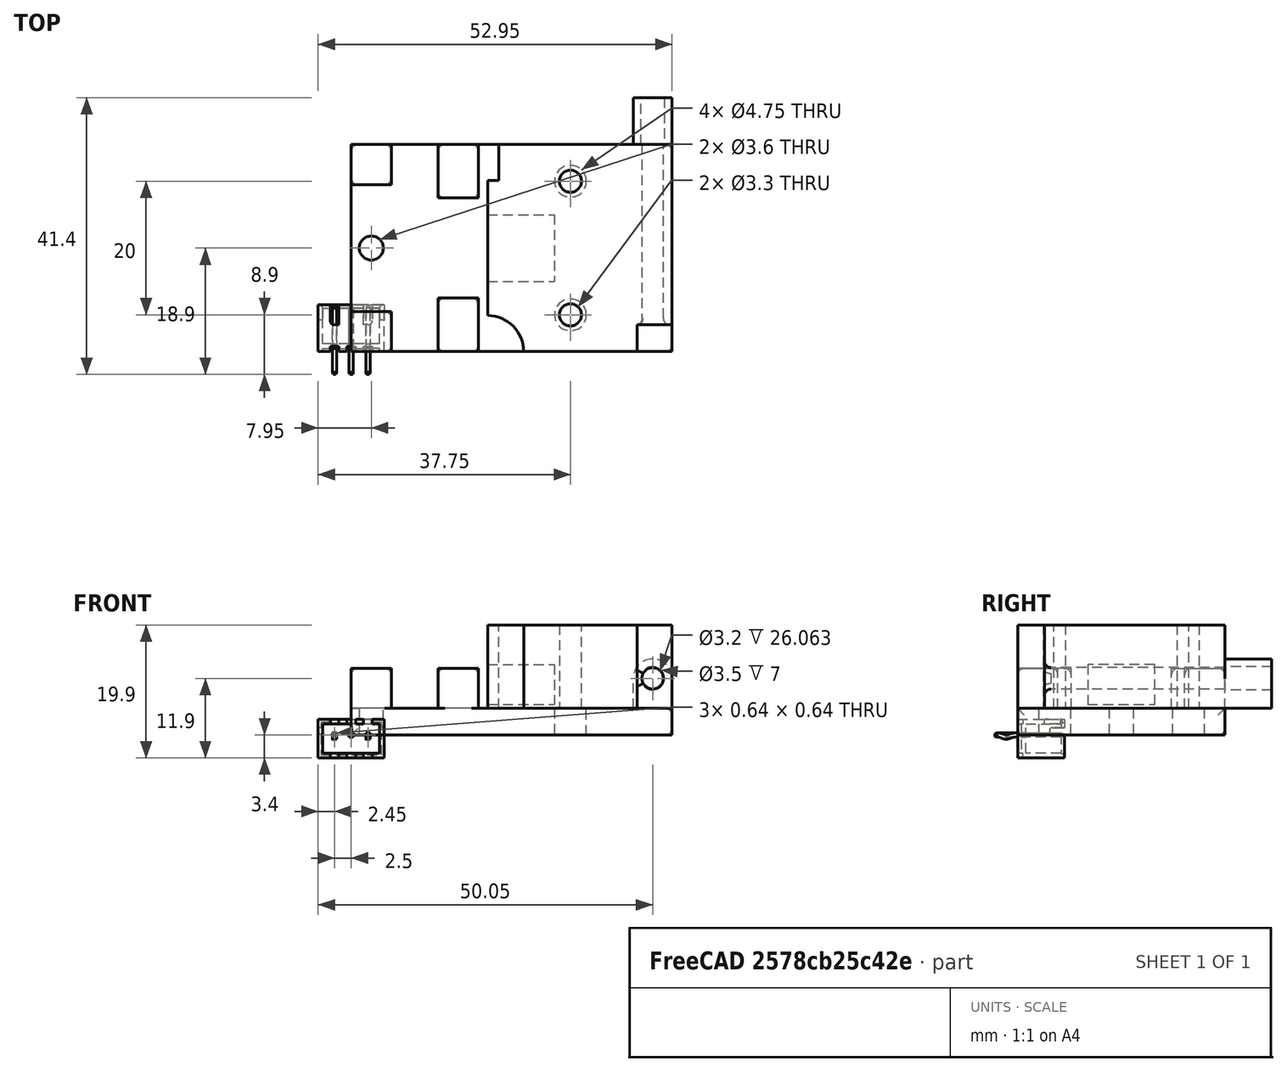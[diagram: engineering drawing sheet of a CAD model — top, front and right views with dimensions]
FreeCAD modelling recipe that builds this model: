
FCSTD DOCUMENT  (FreeCAD 0.19R24291 (Git))
Label: Filament Sensor Mount
License: All rights reserved
LicenseURL: http://en.wikipedia.org/wiki/All_rights_reserved
objects: Sketcher::SketchObject×6, PartDesign::Pad×4, Part::Feature×4, PartDesign::Body×2, PartDesign::Pocket×2, Mesh::Feature×1, Part::Fillet×1, App::Part×1, PartDesign::Fillet×1
note: 27 computed .brp shape members not serialized (recipe doc carries the construction recipe); baked Part::Feature solids carry a one-line shape summary decoded from their .brp

FEATURE [Mesh::Feature] bowen_retainer
  Placement = pos=(-107.25,-102,0) rot=(0,0,1;0rad)
FEATURE [Sketcher::SketchObject] Sketch
  FullyConstrained = true
  MapMode = 5
  Support = -> [XY_Plane]
  sketch-geometry (9):
    g0: LineSegment StartX=0 StartY=0 StartZ=0 EndX=48 EndY=0 EndZ=0
    g1: LineSegment StartX=48 StartY=0 StartZ=0 EndX=48 EndY=31 EndZ=0
    g2: LineSegment StartX=48 StartY=31 StartZ=0 EndX=0 EndY=31 EndZ=0
    g3: LineSegment StartX=0 StartY=31 StartZ=0 EndX=0 EndY=0 EndZ=0
    g4: Circle CenterX=3 CenterY=15.5 CenterZ=0 NormalX=0 NormalY=0 NormalZ=1 AngleXU=0 Radius=1.8
    g5: Circle CenterX=32.8 CenterY=25.5 CenterZ=0 NormalX=0 NormalY=0 NormalZ=1 AngleXU=0 Radius=2.375
    g6: Circle CenterX=32.8 CenterY=5.5 CenterZ=0 NormalX=0 NormalY=0 NormalZ=1 AngleXU=0 Radius=2.375
    g7: LineSegment StartX=19.5 StartY=31 StartZ=0 EndX=19.5 EndY=0 EndZ=0
    g8: LineSegment StartX=13 StartY=31 StartZ=0 EndX=13 EndY=0 EndZ=0
  constraints (28):
    c: Coincident(g0,g1)
    c: Coincident(g1,g2)
    c: Coincident(g2,g3)
    c: Coincident(g3,g0)
    c: Horizontal(g0)
    c: Horizontal(g2)
    c: Vertical(g1)
    c: Vertical(g3)
    c: Coincident(g0,g-1)
    c: DistanceX(g0,g0) = 48
    c: DistanceY(g1,g1) = 31
    c: Radius(g4) = 1.8
    c: DistanceX(g0,g4) = 3
    c: DistanceY(g0,g4) = 15.5
    c: Radius(g5) = 2.375
    c: Equal(g5,g6)
    c: DistanceX(g6,g0) = 15.2
    c: Vertical(g6,g5)
    c: DistanceY(g6,g5) = 20
    c: DistanceY(g5,g1) = 5.5
    c: PointOnObject(g7,g2)
    c: PointOnObject(g7,g0)
    c: Vertical(g7)
    c: DistanceX(g7,g1) = 28.5
    c: PointOnObject(g8,g2)
    c: PointOnObject(g8,g0)
    c: Vertical(g8)
    c: DistanceX(g2,g8) = 13
FEATURE [PartDesign::Pad] Pad
  Direction = (1,1,1)
  Length = 4
  Length2 = 100
  Profile = -> Sketch
  Type = 0
FEATURE [Sketcher::SketchObject] Sketch001
  ExternalGeometry = -> [Pad]
  FullyConstrained = true
  MapMode = 5
  Placement = pos=(0,0,4) rot=(0,0,1;0rad)
  Support = -> [Pad]
  sketch-geometry (16):
    g0: LineSegment StartX=0 StartY=0 StartZ=0 EndX=6 EndY=0 EndZ=0
    g1: LineSegment StartX=6 StartY=0 StartZ=0 EndX=6 EndY=6 EndZ=0
    g2: LineSegment StartX=6 StartY=6 StartZ=0 EndX=0 EndY=6 EndZ=0
    g3: LineSegment StartX=0 StartY=6 StartZ=0 EndX=0 EndY=0 EndZ=0
    g4: LineSegment StartX=0 StartY=31 StartZ=0 EndX=6 EndY=31 EndZ=0
    g5: LineSegment StartX=6 StartY=31 StartZ=0 EndX=6 EndY=25 EndZ=0
    g6: LineSegment StartX=6 StartY=25 StartZ=0 EndX=0 EndY=25 EndZ=0
    g7: LineSegment StartX=0 StartY=25 StartZ=0 EndX=0 EndY=31 EndZ=0
    g8: LineSegment StartX=13 StartY=31 StartZ=0 EndX=19 EndY=31 EndZ=0
    g9: LineSegment StartX=19 StartY=31 StartZ=0 EndX=19 EndY=23 EndZ=0
    g10: LineSegment StartX=19 StartY=23 StartZ=0 EndX=13 EndY=23 EndZ=0
    g11: LineSegment StartX=13 StartY=23 StartZ=0 EndX=13 EndY=31 EndZ=0
    g12: LineSegment StartX=13 StartY=0 StartZ=0 EndX=19 EndY=0 EndZ=0
    g13: LineSegment StartX=19 StartY=0 StartZ=0 EndX=19 EndY=8 EndZ=0
    g14: LineSegment StartX=19 StartY=8 StartZ=0 EndX=13 EndY=8 EndZ=0
    g15: LineSegment StartX=13 StartY=8 StartZ=0 EndX=13 EndY=0 EndZ=0
  constraints (47):
    c: Coincident(g0,g1)
    c: Coincident(g1,g2)
    c: Coincident(g2,g3)
    c: Coincident(g3,g0)
    c: Horizontal(g0)
    c: Horizontal(g2)
    c: Vertical(g1)
    c: Vertical(g3)
    c: Coincident(g0,g-1)
    c: Coincident(g4,g5)
    c: Coincident(g5,g6)
    c: Coincident(g6,g7)
    c: Coincident(g7,g4)
    c: Horizontal(g4)
    c: Horizontal(g6)
    c: Vertical(g5)
    c: Vertical(g7)
    c: Coincident(g4,g-3)
    c: DistanceX(g0,g0) = 6
    c: Equal(g0,g3)
    c: Equal(g3,g7)
    c: Equal(g7,g4)
    c: Coincident(g8,g9)
    c: Coincident(g9,g10)
    c: Coincident(g10,g11)
    c: Coincident(g11,g8)
    c: Horizontal(g8)
    c: Horizontal(g10)
    c: Vertical(g9)
    c: Vertical(g11)
    c: PointOnObject(g8,g-3)
    c: Coincident(g12,g13)
    c: Coincident(g13,g14)
    c: Coincident(g14,g15)
    c: Coincident(g15,g12)
    c: Horizontal(g12)
    c: Horizontal(g14)
    c: Vertical(g13)
    c: Vertical(g15)
    c: PointOnObject(g12,g-1)
    c: DistanceY(g15,g15) = 8
    c: Equal(g0,g12)
    c: Equal(g12,g8)
    c: Equal(g15,g11)
    c: DistanceX(g4,g8) = 13
    c: Vertical(g10,g14)
    c: DistanceX(g9,g-3) = 29
FEATURE [PartDesign::Pad] Pad001
  BaseFeature = -> Pad
  Direction = (1,1,1)
  Length = 6
  Length2 = 100
  Profile = -> Sketch001
  Type = 0
FEATURE [PartDesign::Body] Body  label="Filament Sensor Mount"
  Group = -> [Sketch,Pad,Sketch001,Pad001]
  Origin = -> Origin
  Tip = -> Pad001
FEATURE [Part::Fillet] Fillet
  Base = -> Pad001
  Edges = 38 edges r=1: [Edge2,Edge3,Edge13,Edge14,Edge15,Edge16,Edge20,Edge21,Edge22,Edge38,Edge39,Edge40,Edge43,Edge44,Edge45,Edge46,Edge47,Edge51,Edge52,Edge53,Edge54,Edge55,Edge56,Edge57,Edge58,Edge59,Edge60,Edge61,Edge62,Edge63,Edge64,Edge65,Edge66,Edge67,Edge68,Edge69,Edge70,Edge71]
FEATURE [Sketcher::SketchObject] Sketch002
  FullyConstrained = true
  MapMode = 5
  Support = -> [XY_Plane001]
  sketch-geometry (11):
    g0: LineSegment StartX=5.4 StartY=2e-16 StartZ=0 EndX=22.4 EndY=2e-16 EndZ=0
    g1: LineSegment StartX=27.6 StartY=4 StartZ=0 EndX=27.6 EndY=31 EndZ=0
    g2: LineSegment StartX=27.6 StartY=31 StartZ=0 EndX=1.7 EndY=31 EndZ=0
    g3: LineSegment StartX=-3.3e-15 StartY=25.6 StartZ=0 EndX=-3.3e-15 EndY=5.4 EndZ=0
    g4: Circle CenterX=12.4 CenterY=25.5 CenterZ=0 NormalX=0 NormalY=0 NormalZ=1 AngleXU=0 Radius=1.65
    g5: Circle CenterX=12.4 CenterY=5.5 CenterZ=0 NormalX=0 NormalY=0 NormalZ=1 AngleXU=0 Radius=1.65
    g6: LineSegment StartX=22.4 StartY=2e-16 StartZ=0 EndX=22.4 EndY=4 EndZ=0
    g7: LineSegment StartX=22.4 StartY=4 StartZ=0 EndX=27.6 EndY=4 EndZ=0
    g8: LineSegment StartX=-3.3e-15 StartY=25.6 StartZ=0 EndX=1.7 EndY=25.6 EndZ=0
    g9: LineSegment StartX=1.7 StartY=25.6 StartZ=0 EndX=1.7 EndY=31 EndZ=0
    g10: ArcOfCircle CenterX=0 CenterY=0 CenterZ=0 NormalX=0 NormalY=0 NormalZ=1 AngleXU=0 Radius=5.4 StartAngle=0 EndAngle=1.5708
  constraints (33):
    c: Coincident(g1,g2)
    c: Horizontal(g0)
    c: Horizontal(g2)
    c: Vertical(g1)
    c: Vertical(g3)
    c: Radius(g4) = 1.65
    c: Equal(g4,g5)
    c: Vertical(g4,g5)
    c: DistanceY(g5,g4) = 20
    c: Vertical(g6)
    c: Coincident(g7,g6)
    c: Horizontal(g7)
    c: Distance(g6) = 4
    c: Coincident(g0,g6)
    c: Coincident(g1,g7)
    c: DistanceX(g7,g7) = 5.2
    c: DistanceY(g-1,g5) = 5.5
    c: DistanceX(g5,g1) = 15.2
    c: Horizontal(g8)
    c: Coincident(g8,g9)
    c: Vertical(g9)
    c: DistanceY(g9,g9) = 5.4
    c: DistanceX(g8,g8) = 1.7
    c: Coincident(g3,g8)
    c: Coincident(g2,g9)
    c: DistanceY(g-1,g2) = 31
    c: DistanceX(g3,g1) = 27.6
    c: DistanceX(g-1,g10) = 5.4
    c: Coincident(g10,g-1)
    c: Coincident(g3,g10)
    c: Coincident(g0,g10)
    c: DistanceX(g0,g0) = 17
    c: PointOnObject(g0,g-1)
FEATURE [PartDesign::Pad] Pad002
  Direction = (1,1,1)
  Length = 12.5
  Length2 = 100
  Profile = -> Sketch002
  Type = 0
FEATURE [Sketcher::SketchObject] Sketch003
  ExternalGeometry = -> [Pad002]
  FullyConstrained = true
  MapMode = 5
  Placement = pos=(0,31,0) rot=(0,0.707107,0.707107;3.14159rad)
  Support = -> [Pad002]
  sketch-geometry (5):
    g0: LineSegment StartX=-27.6 StartY=0 StartZ=0 EndX=-21.8 EndY=0 EndZ=0
    g1: LineSegment StartX=-21.8 StartY=0 StartZ=0 EndX=-21.8 EndY=4.5 EndZ=0
    g2: LineSegment StartX=-27.6 StartY=4.5 StartZ=0 EndX=-27.6 EndY=0 EndZ=0
    g3: ArcOfCircle CenterX=-24.7 CenterY=4.5 CenterZ=0 NormalX=0 NormalY=0 NormalZ=1 AngleXU=0 Radius=2.9 StartAngle=7.1e-15 EndAngle=3.14159
    g4: Circle CenterX=-24.7 CenterY=4.5 CenterZ=0 NormalX=0 NormalY=0 NormalZ=1 AngleXU=0 Radius=1.75
  constraints (14):
    c: Coincident(g0,g1)
    c: Coincident(g2,g0)
    c: Horizontal(g0)
    c: Vertical(g1)
    c: Vertical(g2)
    c: Coincident(g0,g-3)
    c: DistanceX(g0,g0) = 5.8
    c: Coincident(g3,g1)
    c: Angle(g3) = 3.14159
    c: DistanceY(g2,g2) = 4.5
    c: Coincident(g4,g3)
    c: Radius(g4) = 1.75
    c: Coincident(g3,g2)
    c: Horizontal(g1,g2)
FEATURE [PartDesign::Pad] Pad003
  BaseFeature = -> Pad002
  Direction = (1,1,1)
  Length = 7
  Length2 = 100
  Profile = -> Sketch003
  Type = 0
FEATURE [Part::Feature] Part__Feature  label="B3B-XH-A (LF)(SN)"
  shape: bbox 0.64 x 10.2 x 0.96 mm, 28 faces (baked)
FEATURE [Part::Feature] Part__Feature001  label="B3B-XH-A (LF)(SN)001"
  shape: bbox 9.9 x 7 x 5.75 mm, 95 faces (baked)
FEATURE [Part::Feature] Part__Feature002  label="B3B-XH-A (LF)(SN)002"
  shape: bbox 0.64 x 10.2 x 0.96 mm, 26 faces (baked)
FEATURE [Part::Feature] Part__Feature003  label="B3B-XH-A (LF)(SN)003"
  shape: bbox 0.64 x 10.2 x 0.64 mm, 14 faces (baked)
FEATURE [App::Part] B3B_XH_A__LF__SN_  label="B3B-XH-A (LF)(SN)004"
  Group = -> [Part__Feature,Part__Feature001,Part__Feature002,Part__Feature003]
  Origin = -> Origin002
  Placement = pos=(27,15.5,7) rot=(-0.707107,0.707107,0;3.14159rad)
FEATURE [Sketcher::SketchObject] Sketch004
  FullyConstrained = false
  MapMode = 5
  Placement = pos=(-3.3e-15,0,0) rot=(0.57735,-0.57735,-0.57735;2.0944rad)
  Support = -> [Pad003]
  sketch-geometry (4):
    g0: LineSegment StartX=-20.5021 StartY=6.56389 StartZ=0 EndX=-10.4807 EndY=6.56389 EndZ=0
    g1: LineSegment StartX=-10.4807 StartY=6.56389 StartZ=0 EndX=-10.4807 EndY=0.571406 EndZ=0
    g2: LineSegment StartX=-10.4807 StartY=0.571406 StartZ=0 EndX=-20.5021 EndY=0.571406 EndZ=0
    g3: LineSegment StartX=-20.5021 StartY=0.571406 StartZ=0 EndX=-20.5021 EndY=6.56389 EndZ=0
  constraints (8):
    c: Coincident(g0,g1)
    c: Coincident(g1,g2)
    c: Coincident(g2,g3)
    c: Coincident(g3,g0)
    c: Horizontal(g0)
    c: Horizontal(g2)
    c: Vertical(g1)
    c: Vertical(g3)
FEATURE [PartDesign::Pocket] Pocket
  BaseFeature = -> Pad003
  Length = 10
  Length2 = 100
  Profile = -> Sketch004
  Type = 0
FEATURE [Sketcher::SketchObject] Sketch005
  ExternalGeometry = -> [Pocket]
  FullyConstrained = true
  MapMode = 5
  Placement = pos=(0,4,0) rot=(1,0,0;1.5708rad)
  Support = -> [Pocket]
  sketch-geometry (1):
    g0: Circle CenterX=24.7 CenterY=4.5 CenterZ=0 NormalX=0 NormalY=0 NormalZ=1 AngleXU=0 Radius=1.6
  constraints (3):
    c: Radius(g0) = 1.6
    c: DistanceY(g-3,g0) = 4.5
    c: DistanceX(g0,g-3) = 2.9
FEATURE [PartDesign::Pocket] Pocket001
  BaseFeature = -> Pocket
  Length = 30
  Length2 = 100
  Profile = -> Sketch005
  Type = 0
FEATURE [PartDesign::Fillet] Fillet001
  Base = -> Pocket001 [Edge34]
  BaseFeature = -> Pocket001
  Radius = 1
  SupportTransform = false
FEATURE [PartDesign::Body] Body001  label="Filament Sensor"
  Group = -> [Sketch002,Pad002,Sketch003,Pad003,Sketch004,Pocket,Sketch005,Pocket001,Fillet001]
  Origin = -> Origin001
  Placement = pos=(20.4,0,4) rot=(0,0,1;0rad)
  Tip = -> Fillet001
